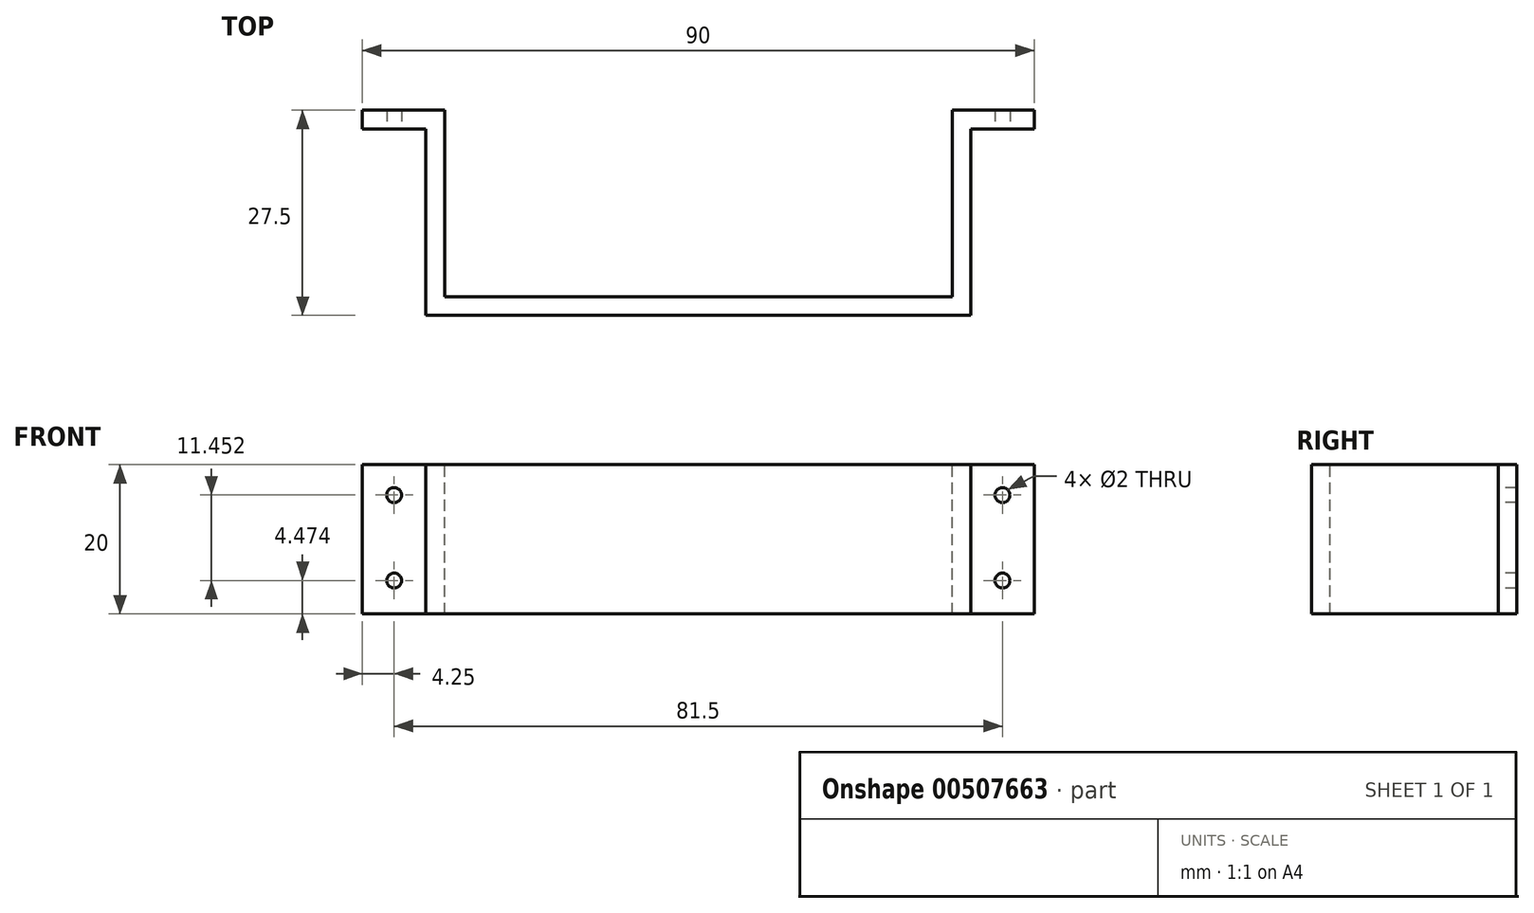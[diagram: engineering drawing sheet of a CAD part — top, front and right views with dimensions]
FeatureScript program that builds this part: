
annotation { "Feature Type Name" : "Feature", "Feature Type Description" : "" }
export const myFeature = defineFeature(function(context is Context, id is Id, definition is map)
    precondition{}
    {
        {
            var Q0;
            Q0=qCreatedBy(makeId("Top.planeOp"),FACE);
            var sketch = newSketch(context, id + "F0", { "sketchPlane" : qUnion([Q0])});
            skLineSegment(sketch, "E0", {"start": v(-34, 0) * mm, "end": v(34, 0) * mm});
            skLineSegment(sketch, "E1", {"start": v(-34, 0) * mm, "end": v(-34, 25) * mm});
            skLineSegment(sketch, "E2", {"start": v(-34, 25) * mm, "end": v(-45, 25) * mm});
            skLineSegment(sketch, "E3", {"start": v(0, 47.83) * mm, "end": v(0, -67.63) * mm, "construction": true});
            skLineSegment(sketch, "E4.MirrorCS", {"start": v(34, 0) * mm, "end": v(34, 25) * mm});
            skLineSegment(sketch, "E5.MirrorCS", {"start": v(34, 25) * mm, "end": v(45, 25) * mm});
            skLineSegment(sketch, "E6.0", {"start": v(36.5, 22.5) * mm, "end": v(45, 22.5) * mm});
            skLineSegment(sketch, "E6.1", {"start": v(-36.5, 22.5) * mm, "end": v(-45, 22.5) * mm});
            skLineSegment(sketch, "E6.2", {"start": v(-36.5, -2.5) * mm, "end": v(-36.5, 22.5) * mm});
            skLineSegment(sketch, "E6.3", {"start": v(-36.5, -2.5) * mm, "end": v(36.5, -2.5) * mm});
            skLineSegment(sketch, "E6.4", {"start": v(36.5, -2.5) * mm, "end": v(36.5, 22.5) * mm});
            skLineSegment(sketch, "E7", {"start": v(-45, 22.5) * mm, "end": v(-45, 25) * mm});
            skLineSegment(sketch, "E8", {"start": v(45, 22.5) * mm, "end": v(45, 25) * mm});
            skSolve(sketch);
        }
        {
            var Q0;
            Q0 = qSketchRegion(id + "F0", true);
            extrude(context, id + "F1", {"entities" : qUnion([Q0]), "oppositeDirection" : true, "depth" : 20 * mm});
        }
        {
            var Q0;
            Q0=makeQuery(id+"F1.opExtrude","SWEPT_FACE",FACE,{"disambiguationData":[OSD([sQuery(id+"F0.wireOp",EDGE,"E6.1")])]});
            var sketch = newSketch(context, id + "F2", { "sketchPlane" : qUnion([Q0])});
            skPoint(sketch, "E9", {"position": v(-40.75, -4.07) * mm});
            skPoint(sketch, "E9.positionSnap0", {"position": v(-40.75, 0) * mm});
            skPoint(sketch, "E10", {"position": v(-40.75, -15.53) * mm});
            skPoint(sketch, "E10.positionSnap0", {"position": v(-40.75, -20) * mm});
            skLineSegment(sketch, "E11", {"start": v(0, 9.87) * mm, "end": v(0, -36.31) * mm, "construction": true});
            skPoint(sketch, "E12.MirrorP", {"position": v(40.75, -4.07) * mm});
            skPoint(sketch, "E13.MirrorP", {"position": v(40.75, -15.53) * mm});
            skSolve(sketch);
        }
        {
            var Q0;
            Q0=sQuery(id+"F2.wireOp",VERTEX,"E9");
            var Q1;
            Q1=sQuery(id+"F2.wireOp",VERTEX,"E10");
            var Q2;
            Q2=sQuery(id+"F2.wireOp",VERTEX,"E12.MirrorP");
            var Q3;
            Q3=sQuery(id+"F2.wireOp",VERTEX,"E13.MirrorP");
            var Q4;
            Q4=makeQuery(id+"F1.opExtrude","SWEPT_BODY",BODY,{"disambiguationData":[OSD([sQuery(id+"F0.wireOp",EDGE,"E0"),sQuery(id+"F0.wireOp",EDGE,"E1"),sQuery(id+"F0.wireOp",EDGE,"E2"),sQuery(id+"F0.wireOp",EDGE,"E4.MirrorCS"),sQuery(id+"F0.wireOp",EDGE,"E5.MirrorCS"),sQuery(id+"F0.wireOp",EDGE,"E6.0"),sQuery(id+"F0.wireOp",EDGE,"E6.1"),sQuery(id+"F0.wireOp",EDGE,"E6.2"),sQuery(id+"F0.wireOp",EDGE,"E6.3"),sQuery(id+"F0.wireOp",EDGE,"E6.4"),sQuery(id+"F0.wireOp",EDGE,"E7"),sQuery(id+"F0.wireOp",EDGE,"E8")])]});
            hole(context, id + "F3", {"style" : HoleStyle.C_SINK, "endStyle" : HoleEndStyle.BLIND, "holeDiameter" : 2 * mm, "cSinkDiameter" : 2 * mm, "cSinkAngle" : 45 * degree, "holeDepth" : 20 * mm, "isTappedThrough" : true, "tappedDepth" : 12 * mm, "tapClearance" : 3, "locations" : qUnion([Q0, Q1, Q2, Q3]), "scope" : qUnion([Q4])});
        }
    });
